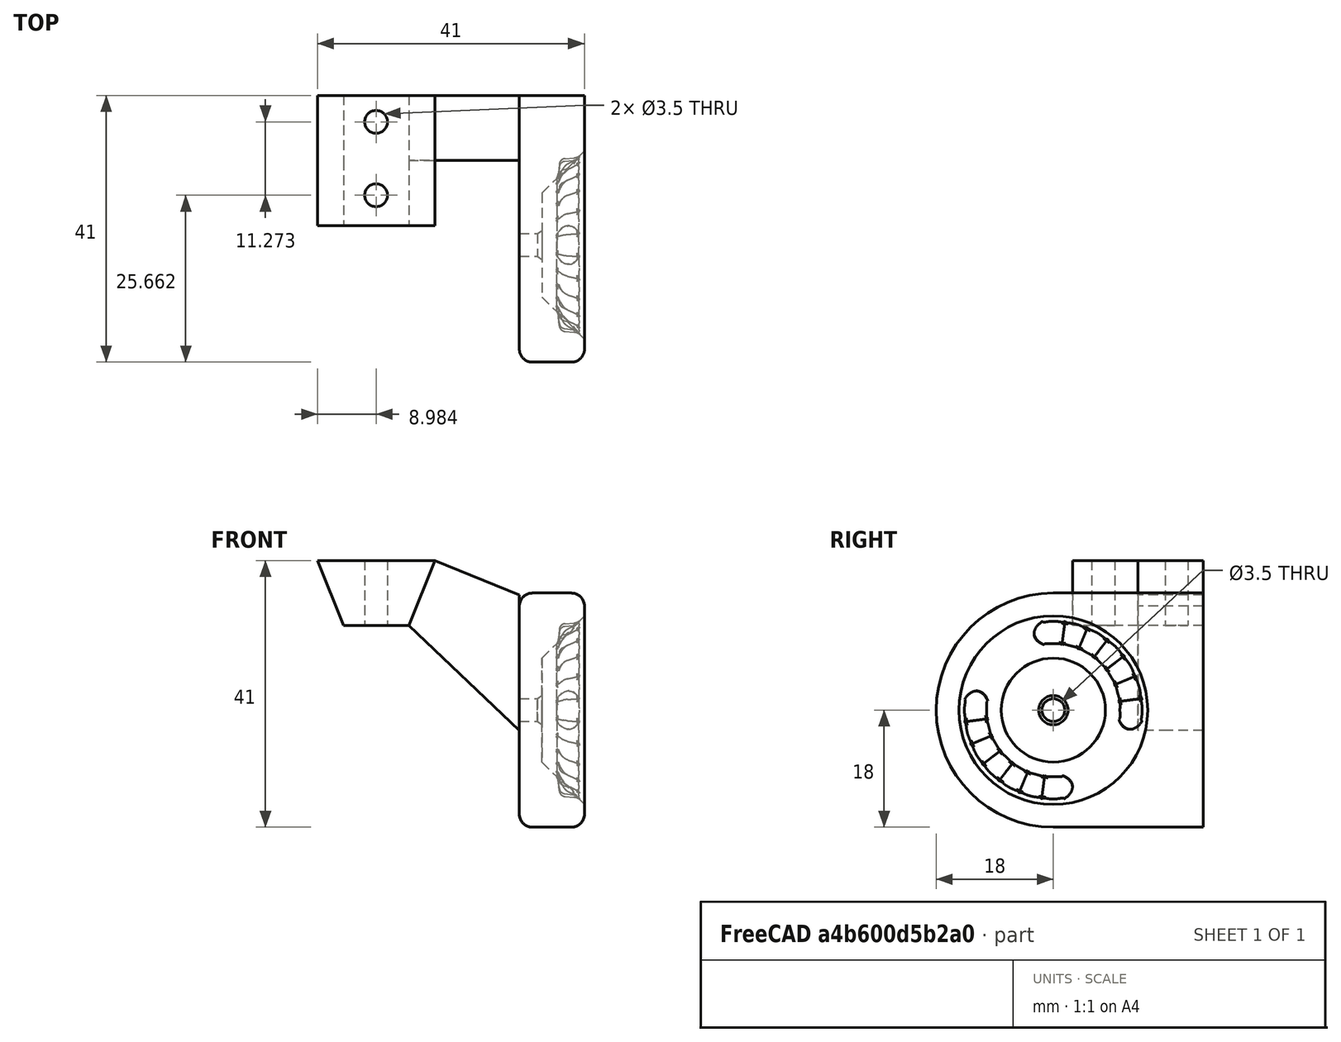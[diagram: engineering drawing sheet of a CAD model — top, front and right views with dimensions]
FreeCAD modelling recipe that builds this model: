
FCSTD DOCUMENT  (FreeCAD 0.18R)
Label: PrusaMini-DisplayMount
License: CreativeCommons Attribution
LicenseURL: http://creativecommons.org/licenses/by/4.0/
objects: Sketcher::SketchObject×5, PartDesign::Body×3, Part::MultiFuse×3, PartDesign::Pad×2, PartDesign::Revolution×2, Part::Cut×2, Part::Fillet×2, PartDesign::Hole×1, PartDesign::PolarPattern×1, Part::Feature×1, Part::Box×1, Part::Cylinder×1, App::Part×1, Mesh::Feature×1
note: 29 computed .brp shape members not serialized (recipe doc carries the construction recipe); baked Part::Feature solids carry a one-line shape summary decoded from their .brp

FEATURE [Sketcher::SketchObject] Sketch010
  Placement = pos=(0,23,0) rot=(1,0,0;1.5708rad)
  Support = -> [XZ_Plane004]
  sketch-geometry (6):
    g0: LineSegment StartX=-9 StartY=0 StartZ=0 EndX=9 EndY=0 EndZ=0
    g1: LineSegment StartX=9 StartY=0 StartZ=0 EndX=22 EndY=-5.25939 EndZ=0
    g2: LineSegment StartX=22 StartY=-5.25939 StartZ=0 EndX=22 EndY=-26.1394 EndZ=0
    g3: LineSegment StartX=22 StartY=-26.1394 StartZ=0 EndX=5 EndY=-10 EndZ=0
    g4: LineSegment StartX=5 StartY=-10 StartZ=0 EndX=-5 EndY=-10 EndZ=0
    g5: LineSegment StartX=-5 StartY=-10 StartZ=0 EndX=-9 EndY=0 EndZ=0
  constraints (14):
    c: Coincident(g0,g1)
    c: Coincident(g1,g2)
    c: Coincident(g2,g3)
    c: Coincident(g3,g4)
    c: Coincident(g4,g5)
    c: Coincident(g0,g5)
    c: DistanceX(g0,g0) = 18
    c: PointOnObject(g-1,g0)
    c: Vertical(g2)
    c: DistanceY(g5,g5) = 10
    c: Symmetric(g4,g3,g-2)
    c: DistanceX(g4,g4) = 10
    c: Symmetric(g0,g0,g-2)
    c: DistanceX(g-1,g1) = 22
FEATURE [PartDesign::Pad] Pad005
  Length = 10
  Length2 = 100
  Placement = pos=(0,0,0) rot=(1,0,0;1.5708rad)
  Profile = -> Sketch010
  Type = 0
FEATURE [Sketcher::SketchObject] Sketch011
  Placement = pos=(0,13,-4e-15) rot=(0.57735,0.57735,-0.57735;2.0944rad)
  Support = -> [Pad005]
  sketch-geometry (4):
    g0: LineSegment StartX=0 StartY=-9 StartZ=0 EndX=10 EndY=-5 EndZ=0
    g1: LineSegment StartX=10 StartY=-5 StartZ=0 EndX=10 EndY=5 EndZ=0
    g2: LineSegment StartX=10 StartY=5 StartZ=0 EndX=0 EndY=9 EndZ=0
    g3: LineSegment StartX=0 StartY=9 StartZ=0 EndX=0 EndY=-9 EndZ=0
  constraints (10):
    c: Coincident(g0,g1)
    c: Coincident(g1,g2)
    c: Coincident(g2,g3)
    c: Coincident(g0,g3)
    c: DistanceX(g0,g0) = 10
    c: PointOnObject(g-1,g3)
    c: DistanceY(g3,g3) = 18
    c: Symmetric(g0,g2,g-1)
    c: Symmetric(g1,g0,g-1)
    c: DistanceY(g1,g1) = 10
FEATURE [PartDesign::Pad] Pad006
  BaseFeature = -> Pad005
  Length = 10
  Length2 = 100
  Placement = pos=(0,0,0) rot=(1,0,0;1.5708rad)
  Profile = -> Sketch011
  Type = 0
FEATURE [Sketcher::SketchObject] Sketch013
  Placement = pos=(0,23,0) rot=(0,0,1;0rad)
  sketch-geometry (2):
    g0: Circle CenterX=-0.015802 CenterY=-4.06545 CenterZ=0 NormalX=0 NormalY=0 NormalZ=1 AngleXU=0 Radius=1.75
    g1: Circle CenterX=-0.015802 CenterY=-15.3384 CenterZ=0 NormalX=0 NormalY=0 NormalZ=1 AngleXU=0 Radius=1.75
  constraints (3):
    c: Radius(g0) = 1.75
    c: Equal(g0,g1)
    c: Vertical(g1,g0)
FEATURE [PartDesign::Hole] Hole001
  BaseFeature = -> Pad006
  Depth = 25
  DepthType = 0
  Diameter = 3.5
  DrillPoint = 1
  DrillPointAngle = 118
  HoleCutCountersinkAngle = 90
  HoleCutDepth = 3
  HoleCutDiameter = 6.3
  HoleCutType = 0
  ModelActualThread = false
  Placement = pos=(0,0,0) rot=(1,0,0;1.5708rad)
  Profile = -> Sketch013
  Tapered = false
  TaperedAngle = 90
  ThreadAngle = 0
  ThreadClass = 0
  ThreadCutOffInner = 0
  ThreadCutOffOuter = 0
  ThreadDirection = 0
  ThreadFit = 0
  ThreadPitch = 0
  ThreadSize = 0
  ThreadType = 0
  Threaded = false
FEATURE [PartDesign::Body] Body002  label="BracketV2"
  Group = -> [Sketch010,Pad005,Sketch011,Pad006,Sketch013,Hole001]
  Origin = -> Origin004
  Tip = -> Hole001
FEATURE [Sketcher::SketchObject] Sketch015
  MapMode = 5
  Support = -> [XY_Plane008]
  sketch-geometry (7):
    g0: LineSegment StartX=0 StartY=1.75 StartZ=0 EndX=2.75 EndY=1.75 EndZ=0
    g1: LineSegment StartX=2.75 StartY=1.75 StartZ=0 EndX=3.5 EndY=2.25 EndZ=0
    g2: LineSegment StartX=3.5 StartY=2.25 StartZ=0 EndX=3.5 EndY=8 EndZ=0
    g3: LineSegment StartX=3.5 StartY=8 StartZ=0 EndX=10 EndY=14.5 EndZ=0
    g4: LineSegment StartX=10 StartY=14.5 StartZ=0 EndX=10 EndY=18 EndZ=0
    g5: LineSegment StartX=10 StartY=18 StartZ=0 EndX=0 EndY=18 EndZ=0
    g6: LineSegment StartX=0 StartY=18 StartZ=0 EndX=0 EndY=1.75 EndZ=0
  constraints (21):
    c: Coincident(g0,g1)
    c: Coincident(g1,g2)
    c: Coincident(g2,g3)
    c: Coincident(g3,g4)
    c: Coincident(g6,g0)
    c: Vertical(g6)
    c: Vertical(g2)
    c: Horizontal(g0)
    c: Horizontal(g5)
    c: Vertical(g4)
    c: DistanceY(g-1,g0) = 1.75
    c: DistanceY(g-1,g2) = 8
    c: DistanceY(g-1,g3) = 14.5
    c: PointOnObject(g0,g-2)
    c: DistanceY(g-1,g5) = 18
    c: DistanceX(g2,g3) = 6.5
    c: DistanceX(g0,g1) = 0.75
    c: DistanceY(g0,g1) = 0.5
    c: DistanceX(g0,g1) = 3.5
    c: Coincident(g4,g5)
    c: Coincident(g6,g5)
FEATURE [PartDesign::Revolution] Revolution
  Angle = 360
  Axis = (1,0,0)
  Base = (0,0,0)
  Profile = -> Sketch015
  ReferenceAxis = -> Sketch015 [H_Axis]
FEATURE [PartDesign::Body] Body005  label="SocketBase"
  Group = -> [Sketch015,Revolution]
  Origin = -> Origin008
  Placement = pos=(-3,0,0) rot=(0,0,1;0rad)
  Tip = -> Revolution
FEATURE [Sketcher::SketchObject] Sketch016
  Placement = pos=(6.5,11.9,0) rot=(0,0,1;0.785398rad)
  Support = -> [XY_Plane009]
  sketch-geometry (6):
    g0: LineSegment StartX=1e-16 StartY=1.55 StartZ=0 EndX=1e-16 EndY=-1 EndZ=0
    g1: LineSegment StartX=1e-16 StartY=-1 StartZ=0 EndX=2.95296 EndY=-1 EndZ=0
    g2: LineSegment StartX=2.95296 StartY=-1 StartZ=0 EndX=2.95296 EndY=0 EndZ=0
    g3: ArcOfCircle CenterX=-2e-16 CenterY=0.55 CenterZ=0 NormalX=0 NormalY=0 NormalZ=1 AngleXU=0 Radius=1 StartAngle=0.879301 EndAngle=1.5708
    g4: LineSegment StartX=0.637689 StartY=1.32029 StartZ=0 EndX=1.67759 EndY=0.459413 EndZ=0
    g5: ArcOfCircle CenterX=2.95296 CenterY=2 CenterZ=0 NormalX=0 NormalY=0 NormalZ=1 AngleXU=0 Radius=2 StartAngle=4.02089 EndAngle=4.71239
  constraints (16):
    c: Coincident(g0,g1)
    c: Coincident(g1,g2)
    c: Vertical(g0)
    c: Vertical(g2)
    c: Horizontal(g1)
    c: DistanceY(g2,g2) = 1
    c: PointOnObject(g0,g-2)
    c: PointOnObject(g2,g-1)
    c: Perpendicular(g0,g3) = 4.71239
    c: Radius(g3) = 1
    c: Tangent(g3,g4) = 1.5708
    c: Distance(g4) = 1.35
    c: Radius(g5) = 2
    c: Tangent(g4,g5) = -1.5708
    c: Perpendicular(g5,g2) = 1.5708
    c: DistanceY(g-1,g0) = 1.55
FEATURE [PartDesign::Revolution] Revolution001
  Angle = 360
  Axis = (-0.707107,0.707107,0)
  Base = (6.5,11.9,0)
  Profile = -> Sketch016
  ReferenceAxis = -> Sketch016 [V_Axis]
  Reversed = true
FEATURE [PartDesign::PolarPattern] PolarPattern
  Angle = 90
  Axis = -> X_Axis009
  BaseFeature = -> Revolution001
  Occurrences = 7
  Originals = -> [Revolution001]
FEATURE [PartDesign::Body] Body006  label="MarkerTop"
  Group = -> [Sketch016,Revolution001,PolarPattern]
  Origin = -> Origin009
  Tip = -> PolarPattern
FEATURE [Part::Feature] Body006001  label="MarkerBottom"
  Placement = pos=(0,0,0) rot=(1,0,0;3.14159rad)
  shape: bbox 6.694 x 20.39 x 20.39 mm, 109 faces (baked)
FEATURE [Part::MultiFuse] Fusion  label="Markers"
  Placement = pos=(-2,0,0) rot=(0,0,1;0rad)
  Shapes = -> [Body006,Body006001]
FEATURE [Part::Cut] Cut  label="PrusaDisplaySocket"
  Base = -> Body005
  Tool = -> Fusion
FEATURE [Part::Box] Box  label="Cube"
  AttacherType = Attacher::AttachEngine3D
  Height = 36
  Length = 10
  Placement = pos=(-3,0,-18) rot=(0,0,1;0rad)
  Width = 23
FEATURE [Part::Cylinder] Cylinder
  Angle = 360
  AttacherType = Attacher::AttachEngine3D
  Height = 10
  Placement = pos=(-3,0,0) rot=(0,1,0;1.5708rad)
  Radius = 18
FEATURE [Part::Cut] Cut001
  Base = -> Box
  Tool = -> Cylinder
FEATURE [Part::MultiFuse] Fusion001  label="SocketBlock"
  Placement = pos=(25,0,-23) rot=(0,0,1;0rad)
  Shapes = -> [Cut,Cut001]
FEATURE [Part::Fillet] Fillet
  Base = -> Fusion001
  Edges = 3 edges r=2: [Edge14,Edge17,Edge20]
FEATURE [Part::Fillet] Fillet001
  Base = -> Fillet
  Edges = 2 edges r=2: [Edge3,Edge17]
FEATURE [Part::MultiFuse] Fusion002  label="DispBracket"
  Shapes = -> [Body002,Fillet001]
FEATURE [App::Part] Part001  label="DisplayMountV2"
  Group = -> [Body002,Body005,Body006,Body006001,Cut001,Cut,Fusion,Cylinder,Box,Fusion001,Fillet,Fillet001,Fusion002]
  Origin = -> Origin002
FEATURE [Mesh::Feature] Mesh  label="DispBracket (Meshed)"
  Placement = pos=(0,0,0) rot=(1,0,0;4.71239rad)
